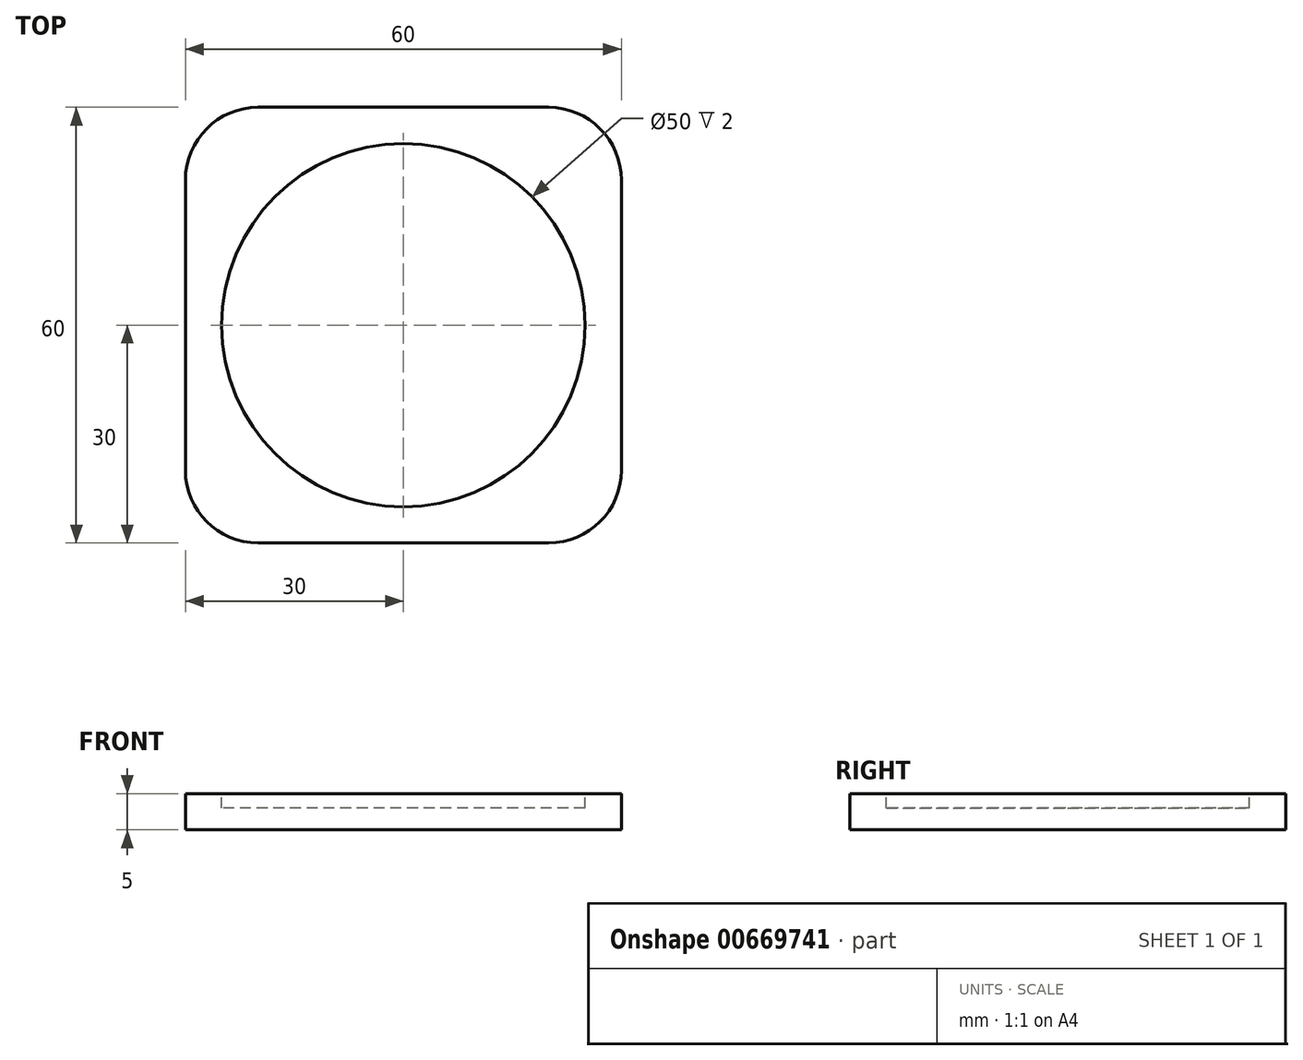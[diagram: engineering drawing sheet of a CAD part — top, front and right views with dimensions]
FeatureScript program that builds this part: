
annotation { "Feature Type Name" : "Feature", "Feature Type Description" : "" }
export const myFeature = defineFeature(function(context is Context, id is Id, definition is map)
    precondition{}
    {
        {
            var Q0;
            Q0=qCreatedBy(makeId("Top.planeOp"),FACE);
            var sketch = newSketch(context, id + "F0", { "sketchPlane" : qUnion([Q0])});
            skLineSegment(sketch, "E0.bottom", {"start": v(30, -30) * mm, "end": v(-30, -30) * mm});
            skLineSegment(sketch, "E0.top", {"start": v(30, 30) * mm, "end": v(-30, 30) * mm});
            skLineSegment(sketch, "E0.left", {"start": v(30, -30) * mm, "end": v(30, 30) * mm});
            skLineSegment(sketch, "E0.right", {"start": v(-30, -30) * mm, "end": v(-30, 30) * mm});
            skPoint(sketch, "E0.middle", {"position": v(0, 0) * mm});
            skSolve(sketch);
        }
        {
            var Q0;
            Q0=makeQuery(id+"F0.imprint","IMPRINT",FACE,{"disambiguationData":[TD([[makeQuery(id+"F0.imprint","IMPRINT",EDGE,{"derivedFrom":sQuery(id+"F0.wireOp",EDGE,"E0.bottom")}),-1.0]])]});
            extrude(context, id + "F1", {"entities" : qUnion([Q0]), "depth" : 5 * mm, "offsetDistance" : 25 * mm});
        }
        {
            var Q0;
            Q0=makeQuery(id+"F1.opExtrude","CAP_FACE",FACE,{"disambiguationData":[OSD([sQuery(id+"F0.wireOp",EDGE,"E0.bottom"),sQuery(id+"F0.wireOp",EDGE,"E0.top"),sQuery(id+"F0.wireOp",EDGE,"E0.left"),sQuery(id+"F0.wireOp",EDGE,"E0.right")])],"isStart":false});
            var sketch = newSketch(context, id + "F2", { "sketchPlane" : qUnion([Q0])});
            skCircle(sketch, "E1", {"center": v(0, 0) * mm, "radius": 25 * mm});
            skSolve(sketch);
        }
        {
            var Q0;
            Q0=makeQuery(id+"F2.imprint","IMPRINT",FACE,{"disambiguationData":[TD([[makeQuery(id+"F2.imprint","IMPRINT",EDGE,{"derivedFrom":sQuery(id+"F2.wireOp",EDGE,"E1")}),1.0]])]});
            extrude(context, id + "F3", {"entities" : qUnion([Q0]), "operationType" : NewBodyOperationType.REMOVE, "oppositeDirection" : true, "depth" : 2 * mm, "offsetDistance" : 25 * mm});
        }
        {
            var Q0;
            Q0=makeQuery(id+"F1.opExtrude","SWEPT_EDGE",EDGE,{"disambiguationData":[OSD([sQuery(id+"F0.wireOp",EDGE,"E0.bottom"),sQuery(id+"F0.wireOp",EDGE,"E0.right")])]});
            var Q1;
            Q1=makeQuery(id+"F1.opExtrude","SWEPT_EDGE",EDGE,{"disambiguationData":[OSD([sQuery(id+"F0.wireOp",EDGE,"E0.top"),sQuery(id+"F0.wireOp",EDGE,"E0.right")])]});
            var Q2;
            Q2=makeQuery(id+"F1.opExtrude","SWEPT_EDGE",EDGE,{"disambiguationData":[OSD([sQuery(id+"F0.wireOp",EDGE,"E0.top"),sQuery(id+"F0.wireOp",EDGE,"E0.left")])]});
            var Q3;
            Q3=makeQuery(id+"F1.opExtrude","SWEPT_EDGE",EDGE,{"disambiguationData":[OSD([sQuery(id+"F0.wireOp",EDGE,"E0.bottom"),sQuery(id+"F0.wireOp",EDGE,"E0.left")])]});
            fillet(context, id + "F4", {"entities" : qUnion([Q0, Q1, Q2, Q3]), "radius" : 10 * mm, "tangentPropagation" : true, "allowEdgeOverflow" : false});
        }
    });
